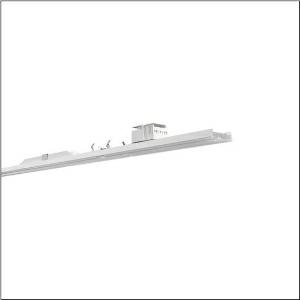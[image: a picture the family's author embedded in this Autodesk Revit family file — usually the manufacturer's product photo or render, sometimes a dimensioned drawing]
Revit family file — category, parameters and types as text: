
# Revit family: licross_r__11_recessed_ho_51tl11cn4cxrd_1146
name_source: partatom
category: Lighting Fixtures
units: mm (PartAtom-declared; Revit-internal decimal feet)

## family parameters
Cut with Voids When Loaded = No
Host = Face
Light Source = No
Part Type = Normal
Room Calculation Point = No
Round Connector Dimension = Use Diameter
Shared = No

## types (1)
- --- (1 x LED, 3400 lm, 21.5 W, 4000K)
    Apparent Load = 22 VA
    CIE Flux Codes = 87 95 99 100 100
    Color Rendering = 80
    Color Temperature = 4000K
    Default Elevation = 1800 mm
    Description = Licross® 11 Recessed HOluminaire insert, length: 1.500mm, width: 66mm, height: 67mm, LED rated luminous flux: 12.100lm, light colour: 840, control gear: ON/OFF Multilumen, CLOi, control gear: ECG Multilumen, with plug, 6-pole, with phase selection, mains connection: 220..240V, AC/DC, 0/50..60Hz, without changeover relay, for emergency light function, for central battery installations according to DIN EN 60598-2-22, halogen-free wiring, primary optical cover: cover, of PMMA, light emission: direct distribution, protection rating (complete): IP40, insulation class (complete): insulation class I (protective earthing), certification: CE, ENEC, VDE, protection symbol: D if used in an environment without relevant dust loads with corresponding accessories, permissible ambient temperature for indoor applications: -35..+35°C, standard: EN 60598-2-22, reducing of maximum allowable ambient temperature of 5°C with ceiling mounting, corresponds to IFS (International Featured Standards) requirements for safety and quality in the food industry, packaging unit: 1 piece
    Height = 58 mm
    Lamp = 1 x LED
    Lamp Light Flux = 3400 lm
    Lamp Power = 21.5 W
    Lamp count = 1
    Length = 1500 mm
    Luminous efficacy = 158 lm/W
    Manufacturer = Siteco
    ModVariant = No
    Model = 51TL11CN4CXRD
    Mounting Place = Ceiling
    Mounting Type = Pendant
    Number of Poles = 1
    OnlyDefault = Yes
    Power Factor = 1
    Product Name = Licross® 11 Recessed HO
    Product group = luminaire insert
    ProductGroupID = 902
    Protection Class = Protection class I
    Protection Degree = IP 40
    RLX_Detail_Level = 1
    RlxData = <blob elided: 20489 chars, md5=09617d4a>
    Socket = socket
    Standby Power = 0 W
    System Light Flux = 3400 lm
    System Power = 22 W
    Type Comments = : DC mode (central or group accumulator) initial emergency light level
    Type Image = l_1266722.jpg
    URL = http://relux.com
    VarID = @adj_134107
    Voltage = 0 V
    Weight = 0.00 kg
    Width = 66 mm

## geometry (parser evidence)
native form markers: Blend x4, Sweep x10
no freeform markers — native parametric forms only
